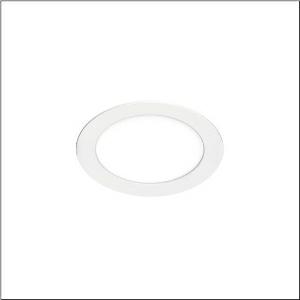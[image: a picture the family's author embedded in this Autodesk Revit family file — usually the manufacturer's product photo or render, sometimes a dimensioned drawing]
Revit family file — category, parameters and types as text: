
# Revit family: lunis_41_flat_51dr10mfgcb
name_source: partatom
category: Lighting Fixtures
units: mm (PartAtom-declared; Revit-internal decimal feet)

## family parameters
Cut with Voids When Loaded = No
Host = Face
Light Source = No
Part Type = Normal
Room Calculation Point = No
Round Connector Dimension = Use Diameter
Shared = No

## types (1)
- --- (1 x LED, 2430 lm, 19.5 W, 4000K)
    Apparent Load = 20 VA
    CIE Flux Codes = 49 80 96 100 100
    Color Rendering = 80
    Color Temperature = 4000K
    Default Elevation = 1800 mm
    Description = Lunis 41,  Flat, downlight, light emission: direct distribution, LED rated luminous flux: 2.360lm, light colour: 830/840, mains connection: 230V, AC, 50/60Hz, housing, round, of aluminium, coated, traffic white (RAL 9016), diameter: 225mm, protection rating (complete): IP20, protection rating (on room side): IP44, insulation class (complete): insulation class II (safety insulation), certification: CE, permissible ambient temperature for indoor applications: -20..+40°C, packaging unit: 1 piece
    Height = 0 mm  [stored 0 ft]
    Lamp = 1 x LED
    Lamp Light Flux = 2430 lm
    Lamp Power = 19.5 W
    Lamp count = 1
    Length = 225 mm
    Luminous efficacy = 125 lm/W
    Manufacturer = Siteco
    ModVariant = No
    Model = 51DR10MFGCB
    Mounting Place = Ceiling
    Mounting Type = Recessed
    Number of Poles = 1
    OnlyDefault = Yes
    Power Factor = 1
    Product Name = Lunis 41 Flat
    Product group = downlight
    ProductGroupID = 400
    Protection Class = Protection class II
    Protection Degree = IP 20
    RLX_Detail_Level = 1
    RLX_Emergency_Light_Flux = 0 lm
    RLX_Emergency_Type = 0
    RLX_Emergency_Type_DB = No
    RlxData = <blob elided: 11581 chars, md5=76e185d1>
    Socket = socket
    Standby Power = 0 W
    System Light Flux = 2430 lm
    System Power = 20 W
    Type Comments = factory setting: colour temperature 4000K
    Type Image = l_1340923.jpg
    URL = http://relux.com
    VarID = @adj_001619
    Voltage = 0 V
    Weight = 0.00 kg
    Width = 0 mm  [stored 0 ft]

note: [stored X ft] marks values corroborated as IEEE doubles in the binary element streams (Revit-internal decimal feet)

## geometry (parser evidence)
native form markers: Sweep x9
no freeform markers — native parametric forms only
